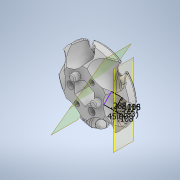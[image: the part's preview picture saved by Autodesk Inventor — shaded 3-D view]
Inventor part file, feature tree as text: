
AUTODESK INVENTOR PART (.ipt)
format: ipt  version: 2020 (Build 240168000, 168)  size: 1,254,400 bytes
history: native  units: in
note: dims shown in document units (in); Inventor stores cm internally (conversion verified against a paired STEP export)
features: sketch x11, extrude x9, chamfer x8, fillet x4, pattern_circular x3, plane x2, other x2, revolve x1, hole x1, mirror x1, projected_geometry x1
ambient origin geometry x8: Origin, YZ Plane, XZ Plane, XY Plane, X Axis, Y Axis, Z Axis, Center Point
bodies: Solid1 (feature_tree)
feature tree (43):
  extrude  "Extrusion1"  Depth=0.5in TaperAngle=0.0deg
  extrude  "Extrusion2"  TaperAngle=0.0deg  [1 undecoded]
  chamfer  "Chamfer1"  Distance=0.0625in Angle=45.0deg
  fillet  "Fillet4"  Radius=0.7874in
  plane  "Work Plane1"
  revolve  "Revolution1"  [1 undecoded]
  pattern_circular  "Circular Pattern1"  Count=6 Angle=360.0deg
  fillet  "Fillet5"  Radius=0.1285in
  pattern_circular  "Circular Pattern3"  [2 undecoded]
  extrude  "Extrusion3"  Depth=0.375in TaperAngle=0.0deg
  hole  "Hole1"  [1 undecoded]
  extrude  "Extrusion4"  Depth=0.375in
  fillet  "Fillet2"  Radius=0.0079in
  fillet  "Fillet1"  Radius=0.0079in
  pattern_circular  "Circular Pattern4"  [2 undecoded]
  extrude  "Extrusion5"  Depth=0.375in
  extrude  "Extrusion6"  Depth=0.375in
  extrude  "Extrusion7"  Depth=0.375in
  extrude  "Extrusion8"  Depth=0.375in
  plane  "Work Plane2"
  mirror  "Mirror1"
  chamfer  "Chamfer2"  Distance=2.3622in Angle=360.0deg
  chamfer  "Chamfer3"  Distance=2.3622in Angle=360.0deg
  chamfer  "Chamfer4"  Distance=0.17in
  chamfer  "Chamfer5"  Distance=0.375in
  chamfer  "Chamfer6"  Distance=0.15in
  chamfer  "Chamfer7"  Distance=0.1857in
  chamfer  "Chamfer8"  Distance=0.375in
  extrude  "Extrusion9"  Depth=0.375in TaperAngle=0.0deg
  sketch  "Sketch1"  dims[d0=1.8898in d1=0.5in d2=0.0in]
  sketch  "Sketch2"  dims[d3=0.5157in d4=0.0in d5=0.0in d6=0.0625in d7=0.125in d8=45.0deg d9=0.7874in]
  sketch  "Sketch3"  dims[d10=45.0deg d11=0.1157in]
  sketch  "Sketch5"  dims[d12=0.2879in]
  sketch  "Sketch6"  dims[d14=0.1079in]
  sketch  "Sketch7"  dims[d15=90.0deg d16=2.3622in d17=360.0deg d19=0.1285in]
  sketch  "Sketch8"  dims[d20=0.395in]
  sketch  "Sketch9"  dims[d21=0.79in]
  sketch  "Sketch10"  dims[d22=60.0deg]
  sketch  "Sketch11"  dims[d23=0.0in d24=0.0in]
  other  "Work Axis1"
  other  "Work Axis2"
  sketch  "Sketch12"  dims[d25=0.1285in d26=0.75in d27=0.22in d28=0.25in d29=0.5635in d30=1.0in d31=0.8108in d32=0.25in d33=0.2344in d34=0.0in d35=0.02in d39=0.5122in d40=0.0079in d41=0.0in d42=0.0079in d43=0.0in d44=0.1526in d45=0.005in d48=0.05in d49=0.0079in d50=0.05in d51=2.3622in d52=360.0deg d54=2.3622in d55=360.0deg d57=0.17in d58=0.375in d59=0.15in d60=0.0in d61=0.1857in d62=0.375in d63=0.16in d64=0.0in d65=0.025in d66=0.125in d67=45.0deg d68=0.35in d69=0.25in d70=45.0deg d71=0.35in d72=0.25in d73=45.0deg d74=0.35in d75=0.25in d76=45.0deg d77=0.35in d78=0.25in d79=45.0deg d80=0.35in d81=0.25in d82=45.0deg d83=0.35in d84=0.25in d85=45.0deg d86=0.0039in d87=0.0in d88=0.5in d89=0.0344in]
  projected_geometry  "Projected Loop1"
note: 7 required parameter values undecoded (feature->parameter linkage not recoverable at this tier; creation-order binding heuristic only, values carry confidence <= 0.55)